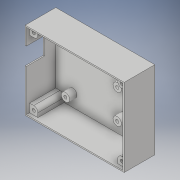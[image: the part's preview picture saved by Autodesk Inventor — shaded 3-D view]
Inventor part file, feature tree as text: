
AUTODESK INVENTOR PART (.ipt)
format: ipt  version: 2019 (Build 230136000, 136)  size: 225,792 bytes
history: native  units: mm
features: other x8, extrude x5, hole x1, loft x1, sketch x1
ambient origin geometry x8: Origin, YZ Plane, XZ Plane, XY Plane, X Axis, Y Axis, Z Axis, Center Point
bodies: Solid1 (feature_tree)
feature tree (16):
  extrude  "Extrusion1"  Depth=72.0mm
  other  "Steny"
  other  "Uchyt_arduino"
  other  "Stena_RJ45"
  other  "Spojeni_srouby"
  extrude  "Extrusion2"  Depth=1.2mm TaperAngle=0.0deg
  extrude  "Extrusion3"  Depth=1.2mm
  extrude  "Extrusion4"  Depth=16.8mm
  extrude  "Extrusion5"  Depth=1.2mm
  hole  "Hole1"  [1 undecoded]
  other  "napajeni_znacka1"
  other  "napajeni_znacka2_rovina"
  loft  "Loft1"
  other  "Zakladna"
  sketch  "Sketch6"  dims[d0=92.0mm d1=72.0mm d2=1.2mm d3=0.0mm d15=1.2mm d16=16.8mm d17=1.2mm d18=1.2mm d19=1.2mm d20=1.2mm d21=1.2mm d23=1.2mm d31=8.0mm d32=3.0mm d33=8.0mm d34=3.0mm d35=8.0mm d36=3.0mm d37=8.0mm d38=3.0mm d39=8.0mm d40=3.0mm d41=8.0mm d42=3.0mm d44=7.0mm d45=0.0mm d46=28.0mm d47=1.2mm d48=0.0mm d49=0.0mm d50=10.9mm d51=1.2mm d52=0.0mm d53=0.0mm d54=25.0mm d55=0.0mm d56=3.0mm d57=6.0mm d58=4.0mm d59=2.0mm d60=90.0deg d61=8.0mm d62=20.594885mm d65=0.7mm d66=-0.5mm d67=0.0mm d68=90.0deg d69=0.0mm d70=90.0deg]
  other  "napajeni_znacka2"
note: 1 required parameter value undecoded (feature->parameter linkage not recoverable at this tier; creation-order binding heuristic only, values carry confidence <= 0.55)
